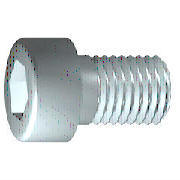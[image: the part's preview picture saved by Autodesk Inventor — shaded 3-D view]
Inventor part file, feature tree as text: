
AUTODESK INVENTOR PART (.ipt)
format: ipt  version: 2017 (Build 210142000, 142)  size: 183,808 bytes
history: native  units: mm (DEFAULTED — no unit token found)
features: sketch x2, extrude x1, plane x1, fillet x1
ambient origin geometry x7: Origin, YZ Plane, XY Plane, X Axis, Y Axis, Z Axis, Center Point
bodies: Solid1 (feature_tree), Body (feature_tree)
feature tree (5):
  extrude  "Slot"  Depth=5.0mm
  plane  "Work Plane1"
  fillet  "Fillet2"  Radius=5.0mm
  sketch  "Sketch1"  dims[d1=22.0mm d2=0.49086mm d3=5.0mm]
  sketch  "Sketch2"  dims[d4=2.5mm d5=60.0deg d6=5.0mm d7=5.0mm d8=4.618802mm d9=8.5mm d10=90.0deg d11=10.0mm d12=0.0mm d13=22.0mm d14=0.0mm d15=0.49076mm d16=0.49076mm d17=0.5mm d19=0.0mm d26=40.0mm d27=45.0deg d28=0.0mm d29=0.0mm d30=0.1mm]
